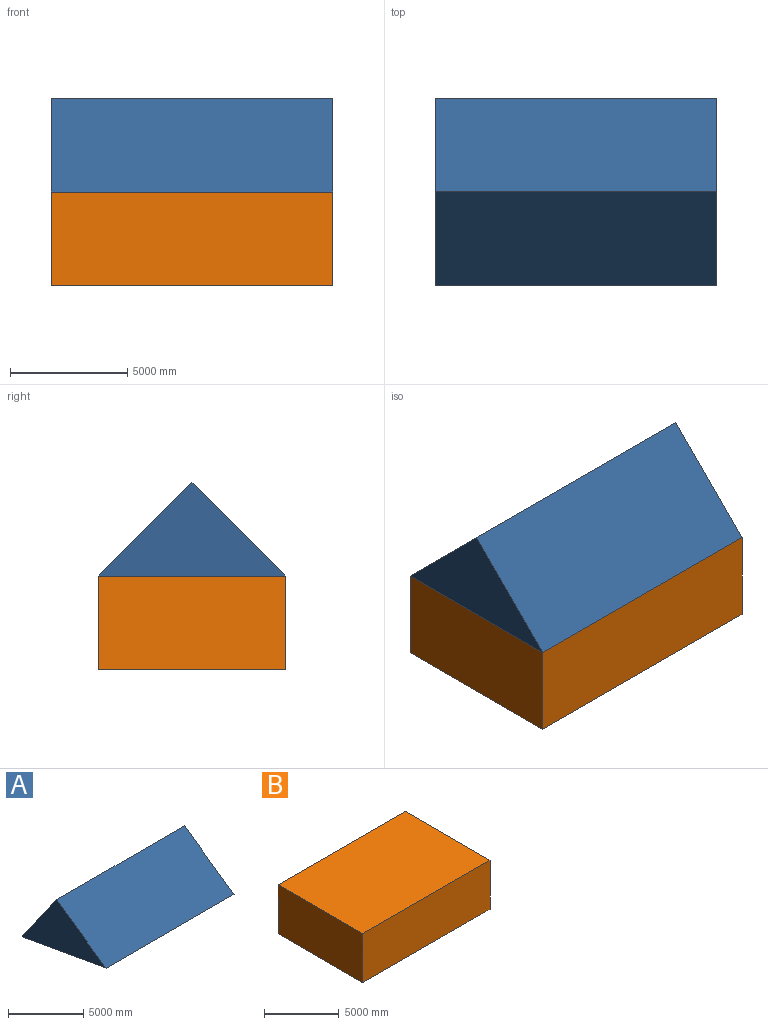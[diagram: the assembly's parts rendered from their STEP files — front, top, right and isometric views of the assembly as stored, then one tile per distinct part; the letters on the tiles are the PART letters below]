
ASSEMBLY  parts=2 mates=1
PART A: 5 faces, bbox 12000x7876.6x4638.2 mm
  f0: plane 12000x7876.59mm, normal (0,-0.17,-0.98), area 96000000mm2, adj f1,f2,f3,f4
  f1: plane 12000x4638.17mm, normal (0,0.82,0.57), area 67882251mm2, adj f0,f2,f3,f4
  f2: plane 12000x4638.17mm, normal (0,-0.57,0.82), area 67882251mm2, adj f0,f1,f3,f4
  f3: plane 7876.59x4638.17mm, normal (1,0,0), area 16000000mm2, adj f0,f1,f2
  f4: plane 7876.59x4638.17mm, normal (-1,0,0), area 16000000mm2, adj f0,f1,f2
PART B: 6 faces, bbox 12000x8000x4000 mm
  f0: plane 12000x8000mm, normal (0,0,1), area 96000000mm2, adj f1,f3,f4,f5
  f1: plane 12000x4000mm, normal (0,-1,0), area 48000000mm2, adj f0,f2,f4,f5
  f2: plane 12000x8000mm, normal (0,0,-1), area 96000000mm2, adj f1,f3,f4,f5
  f3: plane 12000x4000mm, normal (0,1,0), area 48000000mm2, adj f0,f2,f4,f5
  f4: plane 8000x4000mm, normal (1,0,0), area 32000000mm2, adj f0,f1,f2,f3
  f5: plane 8000x4000mm, normal (-1,0,0), area 32000000mm2, adj f0,f1,f2,f3
PLACE A rot(axis=(1,0,0),10.1deg) t=(-2524.54,162.17,1156.59)mm
PLACE B t=(-2524.54,1079.01,-1391.32)mm fixed
MATE fastened A.f0 <-> B.f0  axis (0,0,-1) through (3475.46,1079.01,608.68)mm
